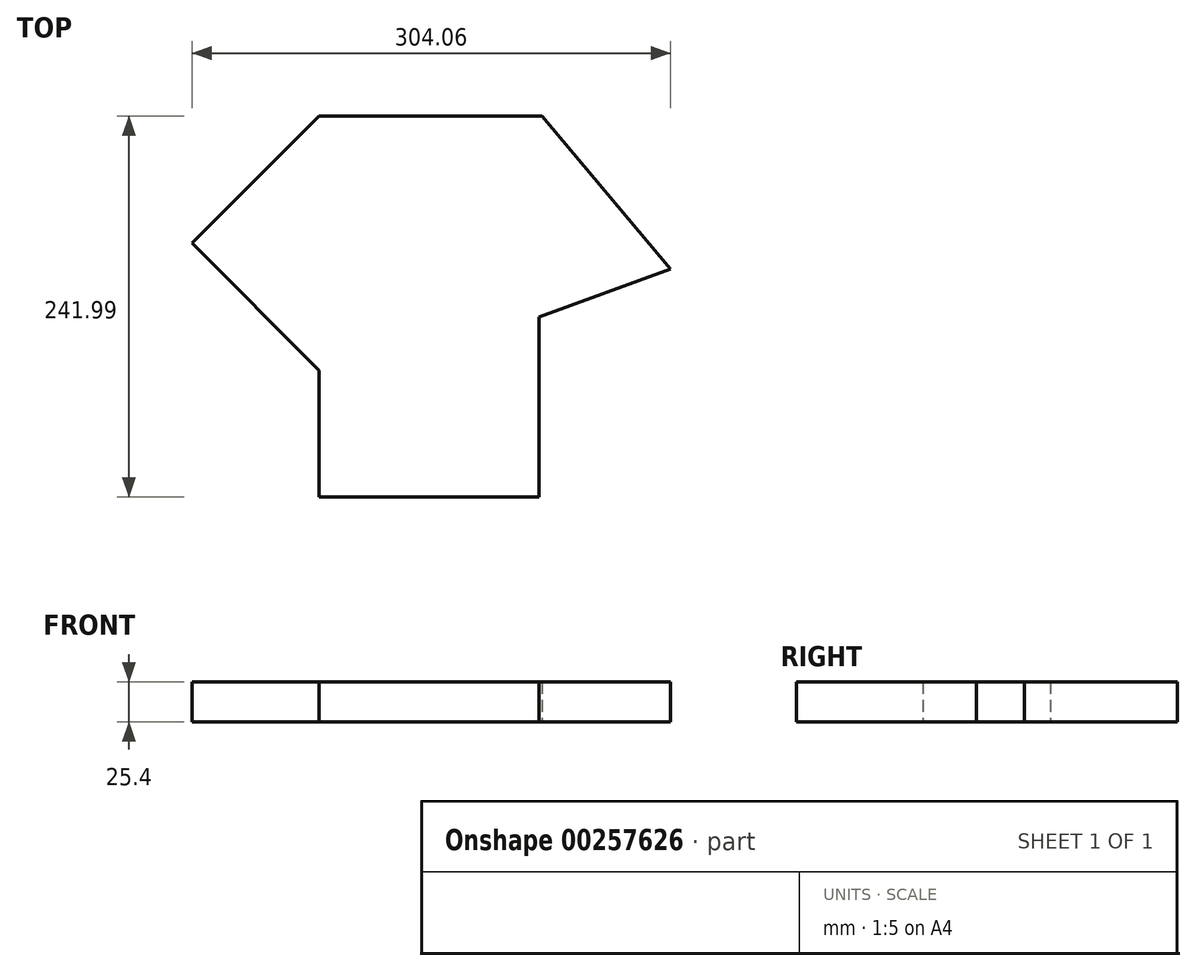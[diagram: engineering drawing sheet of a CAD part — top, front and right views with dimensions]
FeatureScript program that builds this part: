
annotation { "Feature Type Name" : "Feature", "Feature Type Description" : "" }
export const myFeature = defineFeature(function(context is Context, id is Id, definition is map)
    precondition{}
    {
        {
            var Q0;
            Q0=qCreatedBy(makeId("Top.planeOp"),FACE);
            var sketch = newSketch(context, id + "F0", { "sketchPlane" : qUnion([Q0])});
            skLineSegment(sketch, "E0", {"start": v(-66.15, -59.13) * mm, "end": v(73.55, -59.13) * mm});
            skLineSegment(sketch, "E1", {"start": v(73.55, -59.13) * mm, "end": v(73.55, 55.17) * mm});
            skLineSegment(sketch, "E2", {"start": v(73.55, 55.17) * mm, "end": v(157.09, 85.58) * mm});
            skLineSegment(sketch, "E3", {"start": v(157.09, 85.58) * mm, "end": v(75.46, 182.86) * mm});
            skLineSegment(sketch, "E4", {"start": v(-66.15, 182.86) * mm, "end": v(75.46, 182.86) * mm});
            skPoint(sketch, "E5.end.orphan", {"position": v(157.09, 55.17) * mm});
            skLineSegment(sketch, "E6", {"start": v(-66.15, 182.86) * mm, "end": v(-146.97, 102.04) * mm});
            skLineSegment(sketch, "E7", {"start": v(-146.97, 102.04) * mm, "end": v(-66.15, 21.22) * mm});
            skLineSegment(sketch, "E8", {"start": v(-66.15, 21.22) * mm, "end": v(-66.15, -59.13) * mm});
            skSolve(sketch);
        }
        {
            var Q0;
            Q0 = qSketchRegion(id + "F0", true);
            extrude(context, id + "F1", {"entities" : qUnion([Q0]), "depth" : 25.4 * mm});
        }
    });
